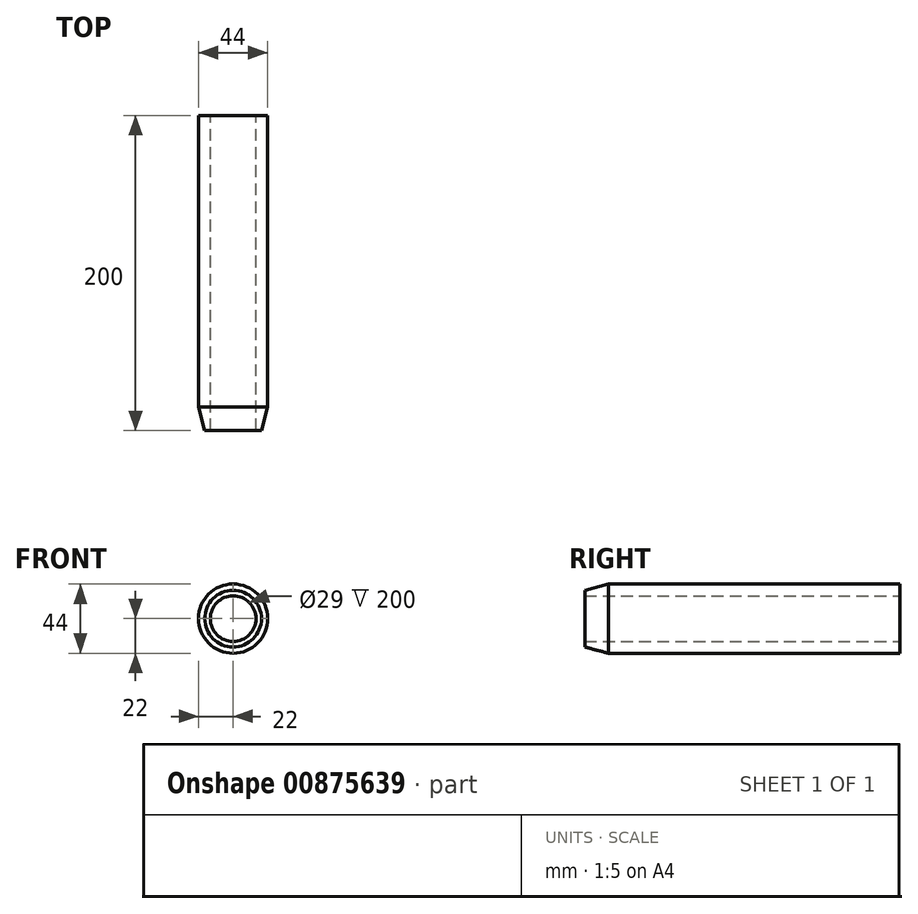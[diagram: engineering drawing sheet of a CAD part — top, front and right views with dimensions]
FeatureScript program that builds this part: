
annotation { "Feature Type Name" : "Feature", "Feature Type Description" : "" }
export const myFeature = defineFeature(function(context is Context, id is Id, definition is map)
    precondition{}
    {
        {
            var Q0;
            Q0=qCreatedBy(makeId("Front.planeOp"),FACE);
            var sketch = newSketch(context, id + "F0", { "sketchPlane" : qUnion([Q0])});
            skCircle(sketch, "E0", {"center": v(0, 0) * mm, "radius": 22 * mm});
            skCircle(sketch, "E1", {"center": v(0, 0) * mm, "radius": 14.5 * mm});
            skSolve(sketch);
        }
        {
            var Q0;
            Q0=makeQuery(id+"F0.imprint","IMPRINT",FACE,{"disambiguationData":[TD([[makeQuery(id+"F0.imprint","IMPRINT",EDGE,{"derivedFrom":sQuery(id+"F0.wireOp",EDGE,"E0")}),1.0]])]});
            extrude(context, id + "F1", {"entities" : qUnion([Q0]), "depth" : 200 * mm, "offsetDistance" : 25 * mm});
        }
        {
            var Q0;
            Q0=makeQuery(id+"F1.opExtrude","CAP_EDGE",EDGE,{"disambiguationData":[OSD([sQuery(id+"F0.wireOp",EDGE,"E0")])],"isStart":false});
            chamfer(context, id + "F2", {"entities" : qUnion([Q0]), "chamferType" : ChamferType.TWO_OFFSETS, "width1" : 4 * mm, "oppositeDirection" : false, "width2" : 15 * mm, "tangentPropagation" : true});
        }
    });
